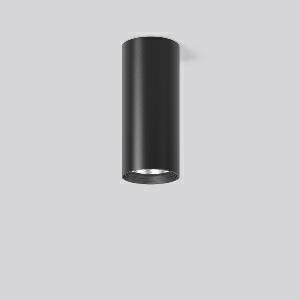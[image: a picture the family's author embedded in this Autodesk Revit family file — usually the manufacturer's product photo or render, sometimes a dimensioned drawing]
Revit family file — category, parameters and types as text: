
# Revit family: heledon_mini_a_931208_003_76_402a
name_source: partatom
category: Lighting Fixtures
units: mm (PartAtom-declared; Revit-internal decimal feet)

## family parameters
Cut with Voids When Loaded = No
Host = Face
Light Source = No
Part Type = Normal
Room Calculation Point = No
Round Connector Dimension = Use Diameter
Shared = No

## types (1)
- HELEDON mini A (1 x LED Modul 930, 3550 lm, 3000)
    Apparent Load = 29 VA
    Approval mark = CE
    CIE Flux Codes = 100 100 100 100 100
    Color Rendering = 90
    Color Temperature = 3000
    Default Elevation = 1800 mm
    Description = Series: HELEDON mini
Cylindrical surface-mounted downlight. Housing: die-cast aluminium, powder-coated. Internal ceiling frame polycarbonate with bayonet mounting. Black plastic ring and recessed LED to prevent glare from the side. Optical assembly with reflector made of MIRO-Silver with 98% total light reflection for outstanding efficiency - can be changed without tools. Best colour rendering index Ra>90. Suitable for Ceiling mounting. Easy installation with a separate ceiling frame with bayonet mounting and plug connection. Driver integrated. Connected via plug-in connector. High quality converter without flickering and stroboscopic effect. The following accessories can be mounted without use of tools: interchangeable lenses, decorative glasses, honeycomb louvre, clear and frosted diffusers, white interchangeable plastic ring. 
Colour: deep black, matt (RAL 9005)
Diameter: 87 mm
Height: 197 mm
Lamp: LED
Socket: without socket
Colour temperature: 3000K
Colour rendering index (CRI): 92
System power: 29 W
Rated luminous flux: 3550 lm
Luminous efficiency: 122 lm/W
Control gear: Converter, dimmable, DALI
Protection class: I
Type of protection: IP 20
    Height = 197 mm
    Lamp = 1 x LED Modul 930
    Lamp Light Flux = 3550 lm
    Lamp count = 1
    Length = 87 mm
    Lifetime = 50000 h
    Luminous efficacy = 122 lm/W
    Manufacturer = RZB
    ModVariant = No
    Model = 931208.003.76
    Mounting Place = Ceiling
    Mounting Type = Surface mounted
    Number of Poles = 1
    OnlyDefault = Yes
    Power Factor = 1
    Product Name = HELEDON mini A
    Product group = Surface mounted downlights
    ProductGroupID = 302
    Protection Class = Protection class I
    Protection Degree = IP 20
    RLX_Detail_Level = 1
    RLX_Emergency_Light_Flux = 0 lm
    RLX_Emergency_Type = 0
    RLX_Emergency_Type_DB = No
    RlxData = <blob elided: 108057 chars, md5=2faf4556>
    Socket = socket
    Standby Power = 0 W
    System Light Flux = 3550 lm
    System Power = 29 W
    Type Comments = Product without accessories
    Type Image = 931188.003.jpg
    URL = http://relux.com
    VarID = ---
    Voltage = 230 V
    Voltage Range = 220-240 V
    Weight = 0.00 kg
    Width = 0 mm  [stored 0 ft]

note: [stored X ft] marks values corroborated as IEEE doubles in the binary element streams (Revit-internal decimal feet)

## geometry (parser evidence)
native form markers: Blend x4, Sweep x9
no freeform markers — native parametric forms only
